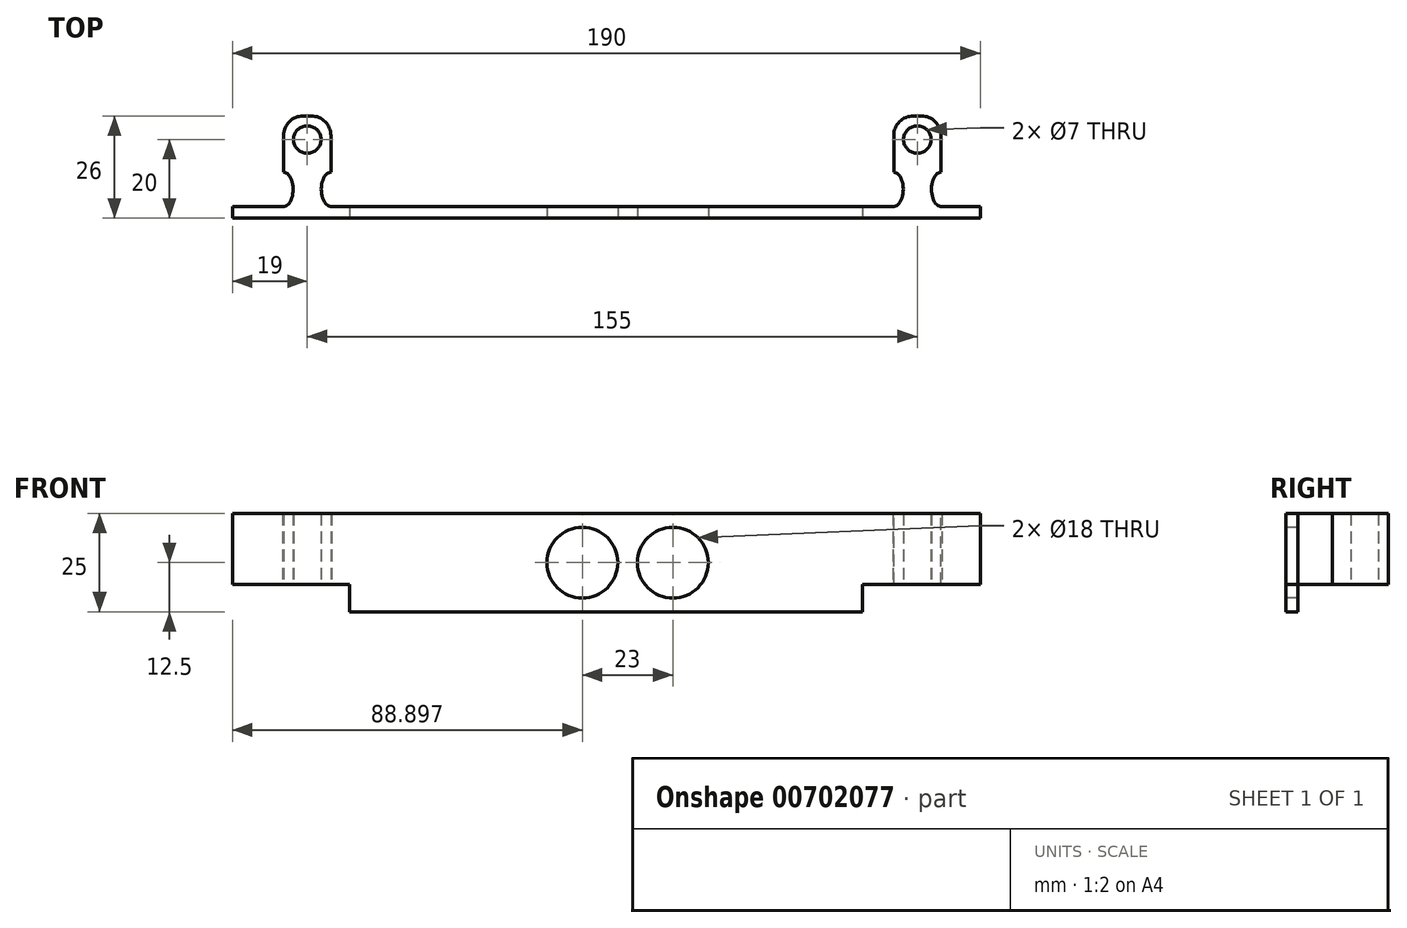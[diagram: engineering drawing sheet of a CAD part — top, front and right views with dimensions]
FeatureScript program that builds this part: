
annotation { "Feature Type Name" : "Feature", "Feature Type Description" : "" }
export const myFeature = defineFeature(function(context is Context, id is Id, definition is map)
    precondition{}
    {
        {
            var Q0;
            Q0=qCreatedBy(makeId("Front.planeOp"),FACE);
            var sketch = newSketch(context, id + "F0", { "sketchPlane" : qUnion([Q0])});
            skLineSegment(sketch, "E0.bottom", {"start": v(-190, 25) * mm, "end": v(0, 25) * mm});
            skLineSegment(sketch, "E0.top", {"start": v(-190, 0) * mm, "end": v(0, 0) * mm});
            skLineSegment(sketch, "E0.left", {"start": v(-190, 25) * mm, "end": v(-190, 0) * mm});
            skLineSegment(sketch, "E0.right", {"start": v(0, 25) * mm, "end": v(0, 0) * mm});
            skSolve(sketch);
        }
        {
            var Q0;
            Q0=makeQuery(id+"F0.imprint","IMPRINT",FACE,{"disambiguationData":[TD([[makeQuery(id+"F0.imprint","IMPRINT",EDGE,{"derivedFrom":sQuery(id+"F0.wireOp",EDGE,"E0.bottom")}),-1.0]])]});
            extrude(context, id + "F1", {"entities" : qUnion([Q0]), "depth" : 3 * mm, "offsetDistance" : 25.4 * mm});
        }
        {
            var Q0;
            Q0=makeQuery(id+"F1.opExtrude","CAP_FACE",FACE,{"disambiguationData":[OSD([sQuery(id+"F0.wireOp",EDGE,"E0.bottom"),sQuery(id+"F0.wireOp",EDGE,"E0.top"),sQuery(id+"F0.wireOp",EDGE,"E0.left"),sQuery(id+"F0.wireOp",EDGE,"E0.right")])],"isStart":false});
            var sketch = newSketch(context, id + "F2", { "sketchPlane" : qUnion([Q0])});
            skCircle(sketch, "E1", {"center": v(-78.1, 12.5) * mm, "radius": 9 * mm});
            skPoint(sketch, "E1.centerSnap0", {"position": v(0, 12.5) * mm});
            skCircle(sketch, "E2", {"center": v(-101.1, 12.5) * mm, "radius": 9 * mm});
            skSolve(sketch);
        }
        {
            var Q0;
            Q0=sQuery(id+"F2.wireOp",VERTEX,"E1.center");
            var Q1;
            Q1=makeQuery(id+"F1.opExtrude","SWEPT_BODY",BODY,{"disambiguationData":[OSD([sQuery(id+"F0.wireOp",EDGE,"E0.bottom"),sQuery(id+"F0.wireOp",EDGE,"E0.top"),sQuery(id+"F0.wireOp",EDGE,"E0.left"),sQuery(id+"F0.wireOp",EDGE,"E0.right")])]});
            hole(context, id + "F3", {"style" : HoleStyle.SIMPLE, "endStyle" : HoleEndStyle.THROUGH, "holeDiameter" : 18 * mm, "majorDiameter" : 6.35 * mm, "isTappedThrough" : true, "tappedDepth" : 12.7 * mm, "tapClearance" : 3, "locations" : qUnion([Q0]), "scope" : qUnion([Q1])});
        }
        {
            var Q0;
            Q0=sQuery(id+"F2.wireOp",VERTEX,"E2.center");
            var Q1;
            Q1=makeQuery(id+"F1.opExtrude","SWEPT_BODY",BODY,{"disambiguationData":[OSD([sQuery(id+"F0.wireOp",EDGE,"E0.bottom"),sQuery(id+"F0.wireOp",EDGE,"E0.top"),sQuery(id+"F0.wireOp",EDGE,"E0.left"),sQuery(id+"F0.wireOp",EDGE,"E0.right")])]});
            hole(context, id + "F4", {"style" : HoleStyle.SIMPLE, "endStyle" : HoleEndStyle.THROUGH, "holeDiameter" : 18 * mm, "majorDiameter" : 6.35 * mm, "isTappedThrough" : true, "tappedDepth" : 12.7 * mm, "tapClearance" : 3, "locations" : qUnion([Q0]), "scope" : qUnion([Q1])});
        }
        {
            var Q0;
            Q0=makeQuery(id+"F1.opExtrude","CAP_FACE",FACE,{"disambiguationData":[OSD([sQuery(id+"F0.wireOp",EDGE,"E0.bottom"),sQuery(id+"F0.wireOp",EDGE,"E0.top"),sQuery(id+"F0.wireOp",EDGE,"E0.left"),sQuery(id+"F0.wireOp",EDGE,"E0.right")])],"isStart":true});
            var sketch = newSketch(context, id + "F5", { "sketchPlane" : qUnion([Q0])});
            skLineSegment(sketch, "E3.bottom", {"start": v(177, 0) * mm, "end": v(165, 0) * mm});
            skLineSegment(sketch, "E3.top", {"start": v(177, 25) * mm, "end": v(165, 25) * mm});
            skLineSegment(sketch, "E3.left", {"start": v(177, 0) * mm, "end": v(177, 25) * mm});
            skLineSegment(sketch, "E3.right", {"start": v(165, 0) * mm, "end": v(165, 25) * mm});
            skLineSegment(sketch, "E4.bottom", {"start": v(22, 0) * mm, "end": v(10, 0) * mm});
            skLineSegment(sketch, "E4.top", {"start": v(22, 25) * mm, "end": v(10, 25) * mm});
            skLineSegment(sketch, "E4.left", {"start": v(10, 0) * mm, "end": v(10, 25) * mm});
            skLineSegment(sketch, "E4.right", {"start": v(22, 0) * mm, "end": v(22, 25) * mm});
            skSolve(sketch);
        }
        {
            var Q0;
            Q0=makeQuery(id+"F5.imprint","IMPRINT",FACE,{"disambiguationData":[TD([[makeQuery(id+"F5.imprint","IMPRINT",EDGE,{"derivedFrom":sQuery(id+"F5.wireOp",EDGE,"E3.bottom")}),-1.0]])]});
            var Q1;
            Q1=makeQuery(id+"F5.imprint","IMPRINT",FACE,{"disambiguationData":[TD([[makeQuery(id+"F5.imprint","IMPRINT",EDGE,{"derivedFrom":sQuery(id+"F5.wireOp",EDGE,"E4.bottom")}),-1.0]])]});
            extrude(context, id + "F6", {"entities" : qUnion([Q0, Q1]), "operationType" : NewBodyOperationType.ADD, "depth" : 23 * mm, "offsetDistance" : 25.4 * mm});
        }
        {
            var Q0;
            Q0=makeQuery(id+"F6.opExtrude","CAP_EDGE",EDGE,{"disambiguationData":[OSD([sQuery(id+"F5.wireOp",EDGE,"E4.left")])],"isStart":false});
            var Q1;
            Q1=makeQuery(id+"F6.opExtrude","CAP_EDGE",EDGE,{"disambiguationData":[OSD([sQuery(id+"F5.wireOp",EDGE,"E4.right")])],"isStart":false});
            var Q2;
            Q2=makeQuery(id+"F6.opExtrude","CAP_EDGE",EDGE,{"disambiguationData":[OSD([sQuery(id+"F5.wireOp",EDGE,"E3.right")])],"isStart":false});
            var Q3;
            Q3=makeQuery(id+"F6.opExtrude","CAP_EDGE",EDGE,{"disambiguationData":[OSD([sQuery(id+"F5.wireOp",EDGE,"E3.left")])],"isStart":false});
            fillet(context, id + "F7", {"entities" : qUnion([Q0, Q1, Q2, Q3]), "radius" : 5 * mm, "tangentPropagation" : true, "allowEdgeOverflow" : false});
        }
        {
            var Q0;
            Q0=makeQuery(id+"F6.boolean.opBoolean","MERGE",FACE,{"derivedFrom":[makeQuery(id+"F1.opExtrude","SWEPT_FACE",FACE,{"disambiguationData":[OSD([sQuery(id+"F0.wireOp",EDGE,"E0.top")])]}),makeQuery(id+"F6.opExtrude","SWEPT_FACE",FACE,{"disambiguationData":[OSD([sQuery(id+"F5.wireOp",EDGE,"E3.bottom")])]}),makeQuery(id+"F6.opExtrude","SWEPT_FACE",FACE,{"disambiguationData":[OSD([sQuery(id+"F5.wireOp",EDGE,"E4.bottom")])]})]});
            var sketch = newSketch(context, id + "F8", { "sketchPlane" : qUnion([Q0])});
            skPoint(sketch, "E5", {"position": v(-16, -17) * mm});
            skPoint(sketch, "E6", {"position": v(-171, -17) * mm});
            skPoint(sketch, "E6.positionSnap0", {"position": v(-171, -23) * mm});
            skSolve(sketch);
        }
        {
            var Q0;
            Q0=sQuery(id+"F8.wireOp",VERTEX,"E5");
            var Q1;
            Q1=sQuery(id+"F8.wireOp",VERTEX,"E6");
            var Q2;
            Q2=makeQuery(id+"F1.opExtrude","SWEPT_BODY",BODY,{"disambiguationData":[OSD([sQuery(id+"F0.wireOp",EDGE,"E0.bottom"),sQuery(id+"F0.wireOp",EDGE,"E0.top"),sQuery(id+"F0.wireOp",EDGE,"E0.left"),sQuery(id+"F0.wireOp",EDGE,"E0.right")])]});
            hole(context, id + "F9", {"style" : HoleStyle.SIMPLE, "endStyle" : HoleEndStyle.THROUGH, "holeDiameter" : 7 * mm, "majorDiameter" : 6.35 * mm, "isTappedThrough" : true, "tappedDepth" : 12.7 * mm, "tapClearance" : 3, "locations" : qUnion([Q0, Q1]), "scope" : qUnion([Q2])});
        }
        {
            var Q0;
            Q0=makeQuery(id+"F6.boolean.opBoolean","MERGE",FACE,{"derivedFrom":[makeQuery(id+"F1.opExtrude","SWEPT_FACE",FACE,{"disambiguationData":[OSD([sQuery(id+"F0.wireOp",EDGE,"E0.top")])]}),makeQuery(id+"F6.opExtrude","SWEPT_FACE",FACE,{"disambiguationData":[OSD([sQuery(id+"F5.wireOp",EDGE,"E3.bottom")])]}),makeQuery(id+"F6.opExtrude","SWEPT_FACE",FACE,{"disambiguationData":[OSD([sQuery(id+"F5.wireOp",EDGE,"E4.bottom")])]})]});
            var sketch = newSketch(context, id + "F10", { "sketchPlane" : qUnion([Q0])});
            skEllipse(sketch, "E7", {"center": v(-22, -4.35) * mm, "majorRadius": 4.37 * mm, "minorRadius": 2.42 * mm, "majorAxis": v(0, -1)});
            skEllipse(sketch, "E8", {"center": v(-10, -4.35) * mm, "majorRadius": 4.37 * mm, "minorRadius": 2.42 * mm, "majorAxis": v(0, -1)});
            skEllipse(sketch, "E9", {"center": v(-177, -4.35) * mm, "majorRadius": 4.37 * mm, "minorRadius": 2.42 * mm, "majorAxis": v(0, -1)});
            skEllipse(sketch, "E10", {"center": v(-165, -4.35) * mm, "majorRadius": 4.37 * mm, "minorRadius": 2.42 * mm, "majorAxis": v(0, -1)});
            skSolve(sketch);
        }
        {
            var Q0;
            {var subQ0=sQuery(id+"F10.wireOp",EDGE,"E8");var subQ1=makeQuery(id+"F6.opExtrude","SWEPT_EDGE",EDGE,{"disambiguationData":[OSD([sQuery(id+"F0.wireOp",EDGE,"E0.top"),sQuery(id+"F5.wireOp",EDGE,"E4.bottom"),sQuery(id+"F5.wireOp",EDGE,"E4.left")])]});var subQ2=makeQuery(id+"F10.imprint","INTERSECT",VERTEX,{"disambiguationData":[OD(0.0)],"derivedFrom":[subQ1,subQ0]});Q0=makeQuery(id+"F10.imprint","IMPRINT",FACE,{"disambiguationData":[TD([[makeQuery(id+"F10.imprint","IMPRINT",EDGE,{"disambiguationData":[TD([[subQ2,-1.0]])],"derivedFrom":subQ0}),1.0]])]});}
            var Q1;
            {var subQ0=sQuery(id+"F10.wireOp",EDGE,"E7");var subQ1=makeQuery(id+"F6.opExtrude","SWEPT_EDGE",EDGE,{"disambiguationData":[OSD([sQuery(id+"F0.wireOp",EDGE,"E0.top"),sQuery(id+"F5.wireOp",EDGE,"E4.bottom"),sQuery(id+"F5.wireOp",EDGE,"E4.right")])]});var subQ2=makeQuery(id+"F10.imprint","INTERSECT",VERTEX,{"disambiguationData":[OD(0.0)],"derivedFrom":[subQ1,subQ0]});Q1=makeQuery(id+"F10.imprint","IMPRINT",FACE,{"disambiguationData":[TD([[makeQuery(id+"F10.imprint","IMPRINT",EDGE,{"disambiguationData":[TD([[subQ2,1.0]])],"derivedFrom":subQ0}),1.0]])]});}
            var Q2;
            {var subQ0=sQuery(id+"F10.wireOp",EDGE,"E10");var subQ1=makeQuery(id+"F6.opExtrude","SWEPT_EDGE",EDGE,{"disambiguationData":[OSD([sQuery(id+"F0.wireOp",EDGE,"E0.top"),sQuery(id+"F5.wireOp",EDGE,"E3.bottom"),sQuery(id+"F5.wireOp",EDGE,"E3.right")])]});var subQ2=makeQuery(id+"F10.imprint","INTERSECT",VERTEX,{"disambiguationData":[OD(0.0)],"derivedFrom":[subQ1,subQ0]});Q2=makeQuery(id+"F10.imprint","IMPRINT",FACE,{"disambiguationData":[TD([[makeQuery(id+"F10.imprint","IMPRINT",EDGE,{"disambiguationData":[TD([[subQ2,-1.0]])],"derivedFrom":subQ0}),1.0]])]});}
            var Q3;
            {var subQ0=sQuery(id+"F10.wireOp",EDGE,"E9");var subQ1=makeQuery(id+"F6.opExtrude","SWEPT_EDGE",EDGE,{"disambiguationData":[OSD([sQuery(id+"F0.wireOp",EDGE,"E0.top"),sQuery(id+"F5.wireOp",EDGE,"E3.bottom"),sQuery(id+"F5.wireOp",EDGE,"E3.left")])]});var subQ2=makeQuery(id+"F10.imprint","INTERSECT",VERTEX,{"disambiguationData":[OD(0.0)],"derivedFrom":[subQ1,subQ0]});Q3=makeQuery(id+"F10.imprint","IMPRINT",FACE,{"disambiguationData":[TD([[makeQuery(id+"F10.imprint","IMPRINT",EDGE,{"disambiguationData":[TD([[subQ2,1.0]])],"derivedFrom":subQ0}),1.0]])]});}
            extrude(context, id + "F11", {"entities" : qUnion([Q0, Q1, Q2, Q3]), "operationType" : NewBodyOperationType.REMOVE, "oppositeDirection" : true, "depth" : 50 * mm, "offsetDistance" : 25.4 * mm});
        }
        {
            var Q0;
            Q0 = qSketchRegion(id + "F10", true);
            extrude(context, id + "F12", {"entities" : qUnion([Q0]), "operationType" : NewBodyOperationType.REMOVE, "oppositeDirection" : true, "depth" : 25.4 * mm, "offsetDistance" : 25.4 * mm});
        }
        {
            var Q0;
            Q0=makeQuery(id+"F2.imprint","IMPRINT",FACE,{"disambiguationData":[TD([[makeQuery(id+"F2.imprint","IMPRINT",EDGE,{"derivedFrom":sQuery(id+"F2.wireOp",EDGE,"E1")}),-1.0]])]});
            var sketch = newSketch(context, id + "F13", { "sketchPlane" : qUnion([Q0])});
            skLineSegment(sketch, "E11.bottom", {"start": v(0, 0) * mm, "end": v(-30, 0) * mm});
            skLineSegment(sketch, "E11.top", {"start": v(0, 7) * mm, "end": v(-30, 7) * mm});
            skLineSegment(sketch, "E11.left", {"start": v(0, 0) * mm, "end": v(0, 7) * mm});
            skLineSegment(sketch, "E11.right", {"start": v(-30, 0) * mm, "end": v(-30, 7) * mm});
            skLineSegment(sketch, "E12.bottom", {"start": v(-190.3, 0) * mm, "end": v(-160.3, 0) * mm});
            skLineSegment(sketch, "E12.top", {"start": v(-190.3, 7) * mm, "end": v(-160.3, 7) * mm});
            skLineSegment(sketch, "E12.left", {"start": v(-190.3, 0) * mm, "end": v(-190.3, 7) * mm});
            skLineSegment(sketch, "E12.right", {"start": v(-160.3, 0) * mm, "end": v(-160.3, 7) * mm});
            skSolve(sketch);
        }
        {
            var Q0;
            Q0=makeQuery(id+"F13.imprint","IMPRINT",FACE,{"disambiguationData":[TD([[makeQuery(id+"F13.imprint","IMPRINT",EDGE,{"derivedFrom":sQuery(id+"F13.wireOp",EDGE,"E11.bottom")}),1.0]])]});
            var Q1;
            {var subQ3=sQuery(id+"F13.wireOp",EDGE,"E12.right");Q1=makeQuery(id+"F13.imprint","IMPRINT",FACE,{"disambiguationData":[TD([[makeQuery(id+"F13.imprint","IMPRINT",EDGE,{"derivedFrom":subQ3}),1.0]])]});}
            extrude(context, id + "F14", {"entities" : qUnion([Q0, Q1]), "operationType" : NewBodyOperationType.REMOVE, "oppositeDirection" : true, "depth" : 70 * mm, "offsetDistance" : 25.4 * mm});
        }
    });
